# Revit family: PX_WHB_LECICO_Ovale- Counter- Top- Basin_PCCTOP022
name_source: partatom
category: Plumbing Fixtures
revit_build: Autodesk Revit 2016 (Build: 20150714_1515(x64)
units: mm (PartAtom-declared; Revit-internal decimal feet)

## family parameters
Always vertical = Yes
Cut with Voids When Loaded = No
Part Type = Normal
Room Calculation Point = No
Round Connector Dimension = Use Diameter
Shared = No
Work Plane-Based = Yes

## types (1)
- Lecico Oval Counter Top Basin
    Code = CTOP022
    Color = White
    Default Elevation = 1200 mm
    Hieght of WHB = 800 mm  [stored 2.62467 ft]
    Manufacturer = LECICO Quality Bathroom Ceramics
    Material = Vitreous China
    Tolani Civil Projects cc = www.tcpbim.co.za
    URL = http://www.lecicosa.co.za
    Weight = 5.50 kg

note: [stored X ft] marks values corroborated as IEEE doubles in the binary element streams (Revit-internal decimal feet)

## geometry (parser evidence)
native form markers: Sweep x3
no freeform markers — native parametric forms only
